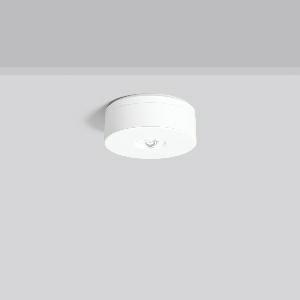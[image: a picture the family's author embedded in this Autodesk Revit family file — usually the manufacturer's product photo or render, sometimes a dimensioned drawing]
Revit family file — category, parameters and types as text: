
# Revit family: lucio_2_672529_002_e0b4
name_source: partatom
category: Lighting Fixtures
units: mm (PartAtom-declared; Revit-internal decimal feet)

## family parameters
Cut with Voids When Loaded = No
Host = Face
Light Source = No
Part Type = Normal
Room Calculation Point = No
Round Connector Dimension = Use Diameter
Shared = No

## types (1)
- Flaechenlinse (1 x LED Modul 740, 310 lm, 4000)
    Apparent Load = 5 VA
    CIE Flux Codes = 45 88 99 100 100
    Color Rendering = 70
    Color Temperature = 4000
    Default Elevation = 1800 mm
    Description = Series: LUCIO 2
Round surface-mounted downlight. For escape route illumination. Housing: plastic (polycarbonate). Cover: polycarbonate. Plastic lenses for area lighting and escape route illumination included in scope of delivery. Suitable for Ceiling mounting. Suitable for connection to central battery systems. 
Colour: white
Diameter: 110 mm
Height: 46 mm
Weight: 0.16 kg
Operating mode: non-maintained power mode
Lamp: LED
Socket: without socket
Colour temperature: 4000K
Colour rendering index (CRI): 70
Luminous flux, emergency: 310 lm
System power, emergency: 4.6 W
Luminous flux, emergency 2: 340 lm
System power, emergency 2: 4.2 W
Control gear: EB
Protection class: II
Type of protection: IP 20
    Height = 46 mm
    Lamp = 1 x LED Modul 740
    Lamp Light Flux = 310 lm
    Lamp count = 1
    Length = 110 mm
    Lifetime = 50000 h
    Luminous efficacy = 67 lm/W
    Manufacturer = RZB
    ModVariant = No
    Model = 672529.002
    Mounting Place = Ceiling
    Mounting Type = Surface mounted
    Number of Poles = 1
    OnlyDefault = Yes
    Power Factor = 1
    Product Name = LUCIO 2
    Product group = Surface mounted ceiling luminaires
    ProductGroupID = 303
    Protection Class = Protection class II
    Protection Degree = IP 20
    RLX_Detail_Level = 1
    RLX_Emergency_Light_Flux = 310 lm
    RLX_Emergency_Type = 3
    RLX_Emergency_Type_DB = Yes
    RlxData = <blob elided: 171345 chars, md5=64068200>
    Socket = socket
    Standby Power = 0 W
    System Light Flux = 310 lm
    System Power = 5 W
    Type Comments = Area lens
    Type Image = 672527.002.jpg
    URL = http://relux.com
    VarID = flaechenlinse
    Voltage = 0 V
    Weight = 0.00 kg
    Width = 0 mm  [stored 0 ft]

note: [stored X ft] marks values corroborated as IEEE doubles in the binary element streams (Revit-internal decimal feet)

## geometry (parser evidence)
native form markers: Blend x4, Sweep x11
no freeform markers — native parametric forms only
